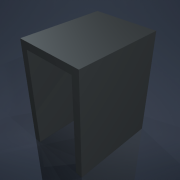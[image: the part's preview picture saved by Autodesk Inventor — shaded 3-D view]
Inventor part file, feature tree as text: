
AUTODESK INVENTOR PART (.ipt)
format: ipt  version: 2022 (Build 260153070, 153G)  size: 168,448 bytes
history: native  units: mm
features: hole x7, sketch x6, other x4, extrude x2
ambient origin geometry x8: Origin, YZ Plane, XZ Plane, XY Plane, X Axis, Y Axis, Z Axis, Center Point
bodies: Body1 (feature_tree)
feature tree (19):
  sketch  "Эскиз1"
  extrude  "Выдавливание3"  Depth=46.0mm
  extrude  "Выдавливание4"  Depth=36.0mm
  other  "РабПлоскость5"
  other  "РабТочка2"
  other  "РабОсь2"
  sketch  "Эскиз3"
  hole  "Отверстие3"  [1 undecoded]
  hole  "Отверстие4"  [1 undecoded]
  hole  "Отверстие5"  [1 undecoded]
  sketch  "Эскиз9"
  hole  "Отверстие7"  [1 undecoded]
  sketch  "Эскиз8"
  hole  "Отверстие9"  [1 undecoded]
  hole  "Отверстие10"  [1 undecoded]
  hole  "Отверстие11"  [1 undecoded]
  sketch  "Эскиз4"
  sketch  "Эскиз5"
  other  "Проецирование ребер1"
note: 7 required parameter values undecoded (feature->parameter linkage not recoverable at this tier; creation-order binding heuristic only, values carry confidence <= 0.55)
